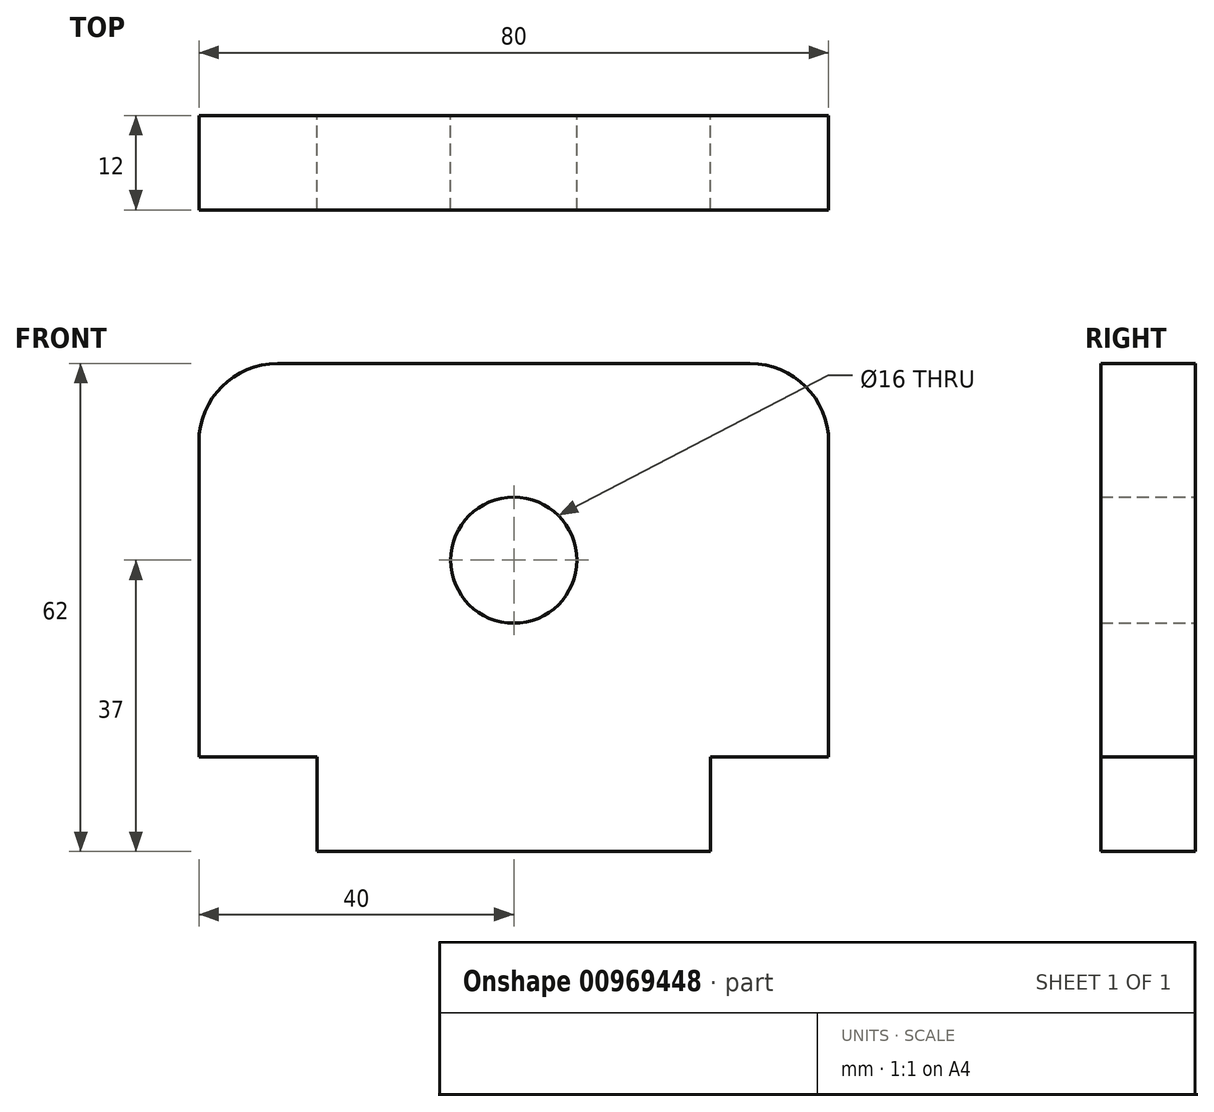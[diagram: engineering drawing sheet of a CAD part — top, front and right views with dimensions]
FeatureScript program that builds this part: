
annotation { "Feature Type Name" : "Feature", "Feature Type Description" : "" }
export const myFeature = defineFeature(function(context is Context, id is Id, definition is map)
    precondition{}
    {
        {
            var Q0;
            Q0=qCreatedBy(makeId("Front.planeOp"),FACE);
            var sketch = newSketch(context, id + "F0", { "sketchPlane" : qUnion([Q0])});
            skLineSegment(sketch, "E0", {"start": v(-40, 0) * mm, "end": v(40, 0) * mm});
            skLineSegment(sketch, "E1", {"start": v(40, 0) * mm, "end": v(40, -50) * mm});
            skLineSegment(sketch, "E2", {"start": v(40, -50) * mm, "end": v(25, -50) * mm});
            skLineSegment(sketch, "E3", {"start": v(25, -50) * mm, "end": v(25, -62) * mm});
            skLineSegment(sketch, "E4", {"start": v(25, -62) * mm, "end": v(-25, -62) * mm});
            skLineSegment(sketch, "E5", {"start": v(-25, -62) * mm, "end": v(-25, -50) * mm});
            skLineSegment(sketch, "E6", {"start": v(-25, -50) * mm, "end": v(-40, -50) * mm});
            skLineSegment(sketch, "E7", {"start": v(-40, -50) * mm, "end": v(-40, 0) * mm});
            skCircle(sketch, "E8", {"center": v(0, -25) * mm, "radius": 8 * mm});
            skSolve(sketch);
        }
        {
            var Q0;
            Q0 = qSketchRegion(id + "F0", true);
            extrude(context, id + "F1", {"entities" : qUnion([Q0]), "depth" : 12 * mm, "offsetDistance" : 25 * mm});
        }
        {
            var Q0;
            Q0=makeQuery(id+"F1.opExtrude","SWEPT_EDGE",EDGE,{"disambiguationData":[OSD([sQuery(id+"F0.wireOp",EDGE,"E0"),sQuery(id+"F0.wireOp",EDGE,"E7")])]});
            var Q1;
            Q1=makeQuery(id+"F1.opExtrude","SWEPT_EDGE",EDGE,{"disambiguationData":[OSD([sQuery(id+"F0.wireOp",EDGE,"E0"),sQuery(id+"F0.wireOp",EDGE,"E1")])]});
            fillet(context, id + "F2", {"entities" : qUnion([Q0, Q1]), "radius" : 10 * mm, "tangentPropagation" : true, "allowEdgeOverflow" : false});
        }
    });
